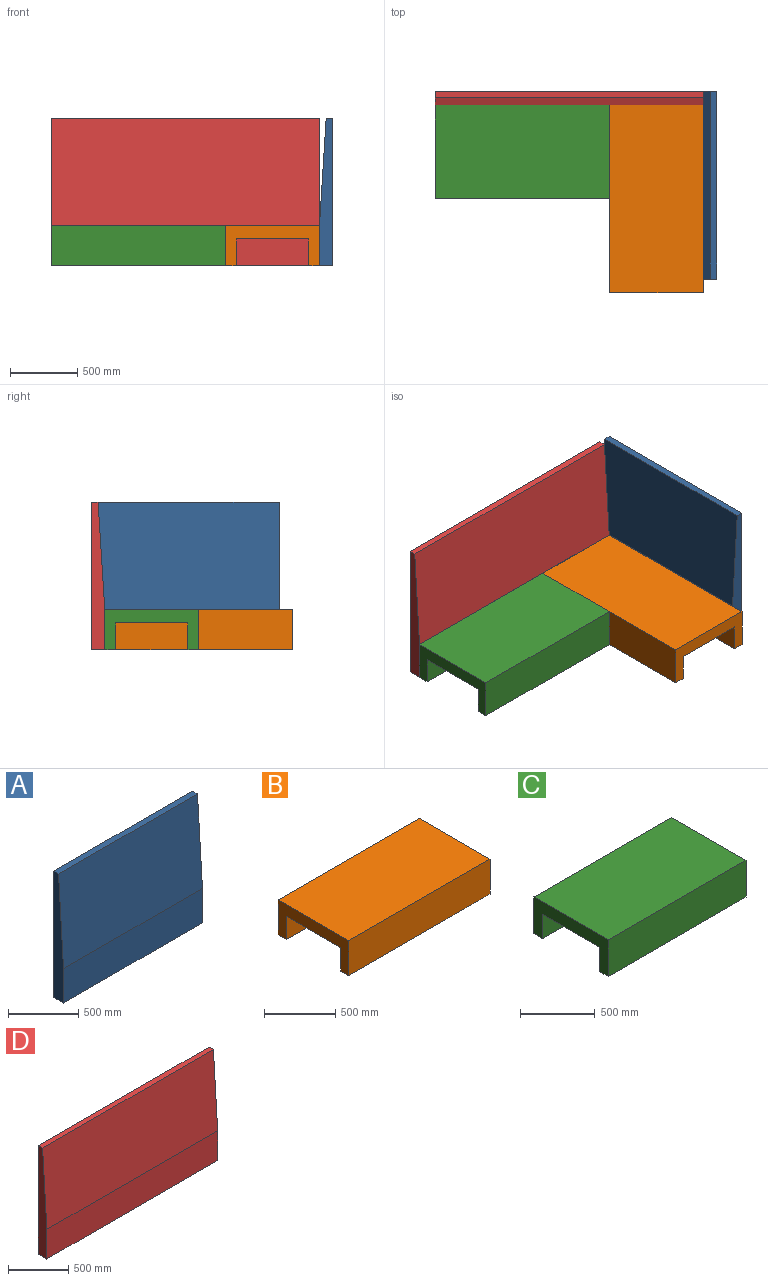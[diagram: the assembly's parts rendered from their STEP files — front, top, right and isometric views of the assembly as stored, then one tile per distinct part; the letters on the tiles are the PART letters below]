
ASSEMBLY  parts=4 mates=9
PART A: 7 faces, bbox 1400x100x1100 mm
  f0: plane 1400x100mm, normal (0,0,-1), area 140000mm2, adj f1,f4,f5,f6
  f1: plane 1400x1100mm, normal (0,1,0), area 1540000mm2, adj f0,f2,f5,f6
  f2: plane 1400x50mm, normal (0,0,1), area 70000mm2, adj f1,f3,f5,f6
  f3: plane 1400x800mm, normal (0,-1,0.06), area 1122185.4mm2, adj f2,f4,f5,f6
  f4: plane 1400x300mm, normal (0,-1,0), area 420000mm2, adj f0,f3,f5,f6
  f5: plane 1100x100mm, normal (1,0,0), area 90000mm2, adj f0,f1,f2,f3,f4
  f6: plane 1100x100mm, normal (-1,0,0), area 90000mm2, adj f0,f1,f2,f3,f4
PART B: 10 faces, bbox 1400x700x300 mm
  f0: plane 1400x300mm, normal (0,-1,0), area 420000mm2, adj f1,f7,f8,f9
  f1: plane 1400x80mm, normal (0,0,-1), area 112000mm2, adj f0,f2,f8,f9
  f2: plane 1400x200mm, normal (0,1,0), area 280000mm2, adj f1,f3,f8,f9
  f3: plane 1400x540mm, normal (0,0,-1), area 756000mm2, adj f2,f4,f8,f9
  f4: plane 1400x200mm, normal (0,-1,0), area 280000mm2, adj f3,f5,f8,f9
  f5: plane 1400x80mm, normal (0,0,-1), area 112000mm2, adj f4,f6,f8,f9
  f6: plane 1400x300mm, normal (0,1,0), area 420000mm2, adj f5,f7,f8,f9
  f7: plane 1400x700mm, normal (0,0,1), area 980000mm2, adj f0,f6,f8,f9
  f8: plane 700x300mm, normal (1,0,0), area 102000mm2, adj f0,f1,f2,f3,f4,f5,f6,f7
  f9: plane 700x300mm, normal (-1,0,0), area 102000mm2, adj f0,f1,f2,f3,f4,f5,f6,f7
PART C: 10 faces, bbox 1300x700x300 mm
  f0: plane 1300x300mm, normal (0,-1,0), area 390000mm2, adj f1,f7,f8,f9
  f1: plane 1300x80mm, normal (0,0,-1), area 104000mm2, adj f0,f2,f8,f9
  f2: plane 1300x200mm, normal (0,1,0), area 260000mm2, adj f1,f3,f8,f9
  f3: plane 1300x540mm, normal (0,0,-1), area 702000mm2, adj f2,f4,f8,f9
  f4: plane 1300x200mm, normal (0,-1,0), area 260000mm2, adj f3,f5,f8,f9
  f5: plane 1300x80mm, normal (0,0,-1), area 104000mm2, adj f4,f6,f8,f9
  f6: plane 1300x300mm, normal (0,1,0), area 390000mm2, adj f5,f7,f8,f9
  f7: plane 1300x700mm, normal (0,0,1), area 910000mm2, adj f0,f6,f8,f9
  f8: plane 700x300mm, normal (1,0,0), area 102000mm2, adj f0,f1,f2,f3,f4,f5,f6,f7
  f9: plane 700x300mm, normal (-1,0,0), area 102000mm2, adj f0,f1,f2,f3,f4,f5,f6,f7
PART D: 7 faces, bbox 2000x100x1100 mm
  f0: plane 2000x100mm, normal (0,0,-1), area 200000mm2, adj f1,f4,f5,f6
  f1: plane 2000x1100mm, normal (0,1,0), area 2200000mm2, adj f0,f2,f5,f6
  f2: plane 2000x50mm, normal (0,0,1), area 100000mm2, adj f1,f3,f5,f6
  f3: plane 2000x800mm, normal (0,-1,0.06), area 1603122mm2, adj f2,f4,f5,f6
  f4: plane 2000x300mm, normal (0,-1,0), area 600000mm2, adj f0,f3,f5,f6
  f5: plane 1100x100mm, normal (1,0,0), area 90000mm2, adj f0,f1,f2,f3,f4
  f6: plane 1100x100mm, normal (-1,0,0), area 90000mm2, adj f0,f1,f2,f3,f4
PLACE A rot(axis=(0,0,-1),90deg) t=(2100,0,0)mm
PLACE B rot(axis=(0,0,1),90deg) t=(2000,-1500,0)mm
PLACE C rot(axis=(0,0,1),180deg) t=(1300,-100,0)mm
PLACE D at identity fixed
MATE planar B.f1 <-> D.f0  axis (0,0,-1) through (1960,-800,0)mm
MATE planar C.f8 <-> D.f6  axis (-1,0,0) through (0,-450,202.94)mm
MATE planar A.f4 <-> B.f0  axis (-1,0,0) through (2000,-1400,150)mm
MATE planar C.f0 <-> D.f4  axis (0,1,0) through (650,-100,150)mm
MATE planar A.f0 <-> D.f0  axis (0,0,-1) through (2050,-700,0)mm
MATE planar B.f8 <-> D.f4  axis (0,1,0) through (1650,-100,202.94)mm
MATE planar B.f0 <-> D.f5  axis (1,0,0) through (2000,-800,150)mm
MATE planar C.f1 <-> D.f0  axis (0,0,-1) through (650,-140,0)mm
MATE planar A.f6 <-> D.f1  axis (0,1,0) through (2000,0,300)mm
